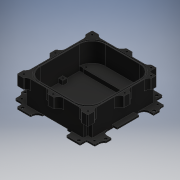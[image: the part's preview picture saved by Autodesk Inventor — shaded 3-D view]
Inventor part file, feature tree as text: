
AUTODESK INVENTOR PART (.ipt)
format: ipt  version: 2018 (Build 220112000, 112)  size: 348,672 bytes
history: native  units: mm
features: fillet x1
ambient origin geometry x8: Origin, YZ Plane, XZ Plane, XY Plane, X Axis, Y Axis, Z Axis, Center Point
bodies: Solid1 (feature_tree)
feature tree (1):
  fillet  "Fillet3"  [1 undecoded]
note: 1 required parameter value undecoded (feature->parameter linkage not recoverable at this tier; creation-order binding heuristic only, values carry confidence <= 0.55)
